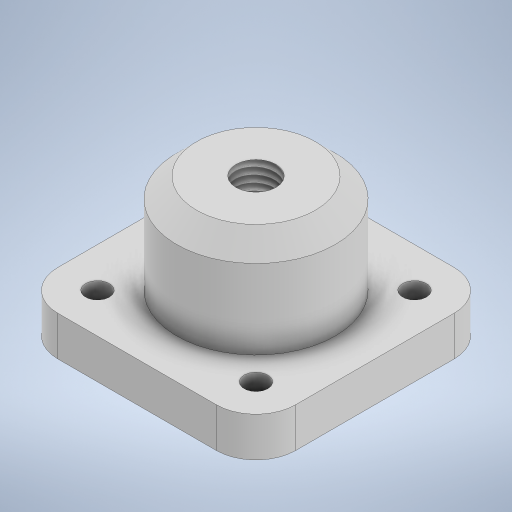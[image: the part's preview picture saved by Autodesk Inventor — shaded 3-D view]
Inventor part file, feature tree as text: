
AUTODESK INVENTOR PART (.ipt)
format: ipt  version: 2023 (Build 270158030, 158C)  size: 285,184 bytes
history: native  units: mm
features: sketch x5, extrude x4, chamfer x1, hole x1
ambient origin geometry x8: Origin, YZ Plane, XZ Plane, XY Plane, X Axis, Y Axis, Z Axis, Center Point
bodies: Solid1 (feature_tree)
feature tree (11):
  extrude  "Extrusion1"  Depth=60.0mm
  extrude  "Extrusion2"  Depth=10.0mm
  chamfer  "Chamfer1"  Distance=10.0mm
  extrude  "Extrusion3"  Depth=25.0mm TaperAngle=0.0deg
  extrude  "Extrusion4"  Depth=20.0mm TaperAngle=0.0deg
  hole  "Hole1"  [1 undecoded]
  sketch  "Sketch1"  dims[d0=60.0mm d1=60.0mm]
  sketch  "Sketch2"  dims[d2=10.0mm d3=6.0mm d4=10.0mm d5=0.0mm]
  sketch  "Sketch3"  dims[d6=40.0mm d7=25.0mm d8=0.0mm]
  sketch  "Sketch4"  dims[d9=5.0mm d10=2.0mm d11=45.0deg d12=20.0mm d13=0.0mm]
  sketch  "Sketch5"  dims[d14=5.0mm d15=0.0mm d16=12.0mm d17=10.106mm d18=24.0mm d19=4.0mm d20=2.0mm d21=90.0deg d22=32.3mm d23=20.594885mm]
note: 1 required parameter value undecoded (feature->parameter linkage not recoverable at this tier; creation-order binding heuristic only, values carry confidence <= 0.55)
